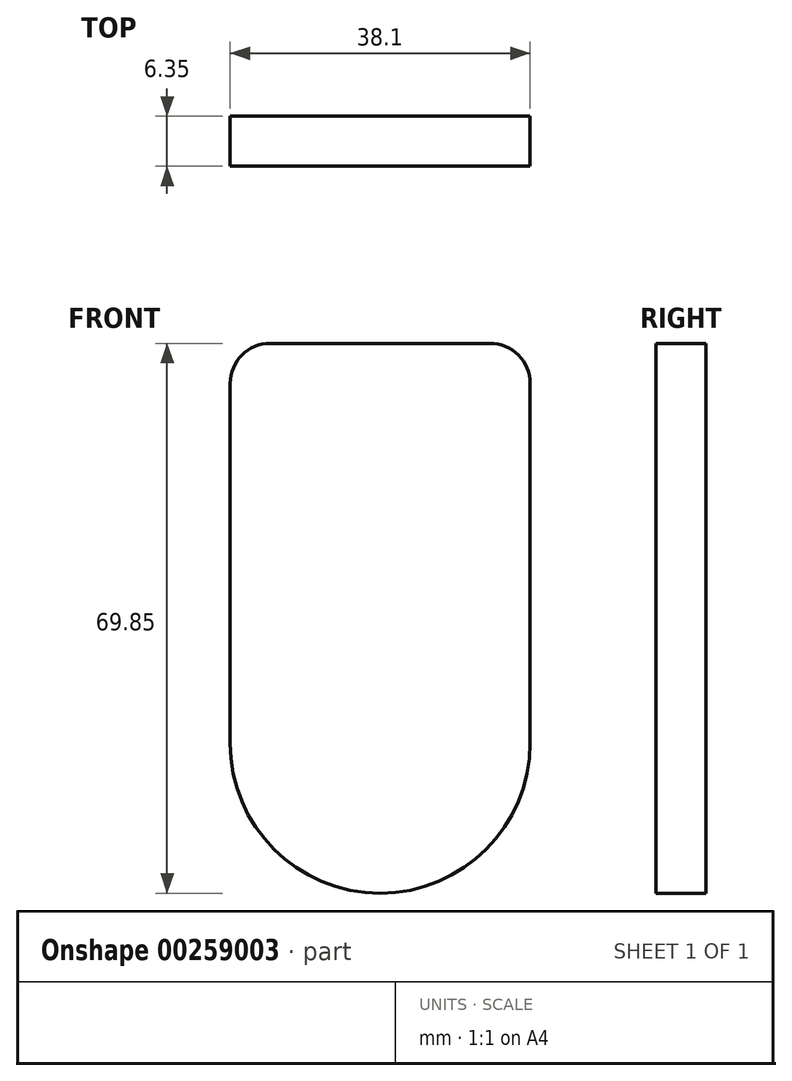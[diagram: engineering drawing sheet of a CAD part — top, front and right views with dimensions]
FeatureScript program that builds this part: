
annotation { "Feature Type Name" : "Feature", "Feature Type Description" : "" }
export const myFeature = defineFeature(function(context is Context, id is Id, definition is map)
    precondition{}
    {
        {
            var Q0;
            Q0=qCreatedBy(makeId("Front.planeOp"),FACE);
            var sketch = newSketch(context, id + "F0", { "sketchPlane" : qUnion([Q0])});
            skArc(sketch, "E0", {"start": v(-19.05, 0) * mm, "mid": v(0, -19.05) * mm, "end": v(19.05, 0) * mm});
            skLineSegment(sketch, "E1", {"start": v(19.05, 0) * mm, "end": v(19.05, 50.8) * mm});
            skLineSegment(sketch, "E2", {"start": v(19.05, 50.8) * mm, "end": v(-19.05, 50.8) * mm});
            skLineSegment(sketch, "E3", {"start": v(-19.05, 50.8) * mm, "end": v(-19.05, 0) * mm});
            skSolve(sketch);
        }
        {
            var Q0;
            Q0=makeQuery(id+"F0.imprint","IMPRINT",FACE,{"disambiguationData":[TD([[makeQuery(id+"F0.imprint","IMPRINT",EDGE,{"derivedFrom":sQuery(id+"F0.wireOp",EDGE,"E0")}),1.0]])]});
            extrude(context, id + "F1", {"entities" : qUnion([Q0]), "depth" : 6.35 * mm});
        }
        {
            var Q0;
            Q0=makeQuery(id+"F1.opExtrude","SWEPT_EDGE",EDGE,{"disambiguationData":[OSD([sQuery(id+"F0.wireOp",EDGE,"E1"),sQuery(id+"F0.wireOp",EDGE,"E2")])]});
            var Q1;
            Q1=makeQuery(id+"F1.opExtrude","SWEPT_EDGE",EDGE,{"disambiguationData":[OSD([sQuery(id+"F0.wireOp",EDGE,"E2"),sQuery(id+"F0.wireOp",EDGE,"E3")])]});
            fillet(context, id + "F2", {"entities" : qUnion([Q0, Q1]), "radius" : 5.08 * mm, "tangentPropagation" : true, "allowEdgeOverflow" : false});
        }
    });
